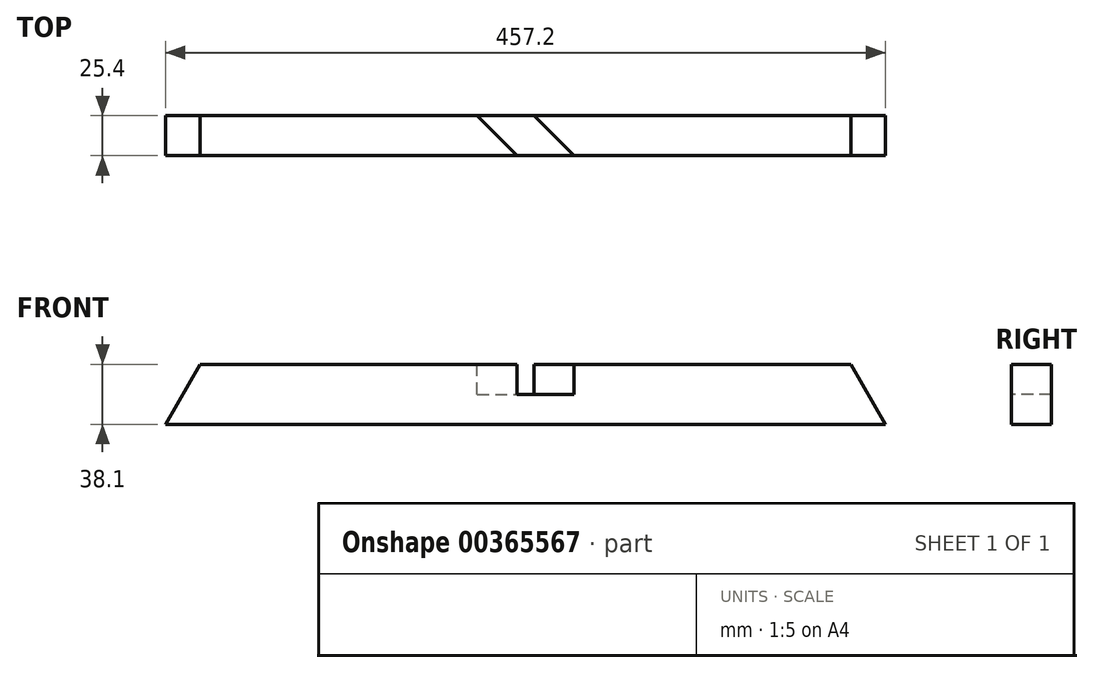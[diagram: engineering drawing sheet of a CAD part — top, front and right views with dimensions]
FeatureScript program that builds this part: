
annotation { "Feature Type Name" : "Feature", "Feature Type Description" : "" }
export const myFeature = defineFeature(function(context is Context, id is Id, definition is map)
    precondition{}
    {
        {
            var Q0;
            Q0=qCreatedBy(makeId("Front.planeOp"),FACE);
            var sketch = newSketch(context, id + "F0", { "sketchPlane" : qUnion([Q0])});
            skLineSegment(sketch, "E0.bottom", {"start": v(0, 0) * mm, "end": v(457.2, 0) * mm});
            skLineSegment(sketch, "E0.top", {"start": v(22, 38.1) * mm, "end": v(435.2, 38.1) * mm});
            skLineSegment(sketch, "E1", {"start": v(0, 0) * mm, "end": v(22, 38.1) * mm});
            skLineSegment(sketch, "E2", {"start": v(457.2, 0) * mm, "end": v(435.2, 38.1) * mm});
            skSolve(sketch);
        }
        {
            var Q0;
            Q0=makeQuery(id+"F0.imprint","IMPRINT",FACE,{"disambiguationData":[TD([[makeQuery(id+"F0.imprint","IMPRINT",EDGE,{"derivedFrom":sQuery(id+"F0.wireOp",EDGE,"E0.bottom")}),1.0]])]});
            extrude(context, id + "F1", {"entities" : qUnion([Q0]), "depth" : 25.4 * mm});
        }
        {
            var Q0;
            Q0=makeQuery(id+"F1.opExtrude","SWEPT_FACE",FACE,{"disambiguationData":[OSD([sQuery(id+"F0.wireOp",EDGE,"E0.top")])]});
            var sketch = newSketch(context, id + "F2", { "sketchPlane" : qUnion([Q0])});
            skLineSegment(sketch, "E3", {"start": v(197.94, 0) * mm, "end": v(223.34, -25.4) * mm});
            skLineSegment(sketch, "E4", {"start": v(223.34, -25.4) * mm, "end": v(259.26, -25.4) * mm});
            skLineSegment(sketch, "E5", {"start": v(259.26, -25.4) * mm, "end": v(233.86, 0) * mm});
            skLineSegment(sketch, "E6", {"start": v(233.86, 0) * mm, "end": v(197.94, 0) * mm});
            skCircle(sketch, "E7", {"center": v(228.6, -12.7) * mm, "radius": 12.7 * mm, "construction": true});
            skSolve(sketch);
        }
        {
            var Q0;
            Q0=makeQuery(id+"F2.imprint","IMPRINT",FACE,{"disambiguationData":[TD([[makeQuery(id+"F2.imprint","IMPRINT",EDGE,{"derivedFrom":sQuery(id+"F2.wireOp",EDGE,"E3")}),1.0]])]});
            var Q1;
            Q1=sQuery(id+"F2.wireOp",EDGE,"E7");
            var Q2;
            Q2=sQuery(id+"F2.wireOp",EDGE,"E5");
            var Q3;
            Q3=sQuery(id+"F2.wireOp",EDGE,"E4");
            var Q4;
            Q4=sQuery(id+"F2.wireOp",EDGE,"E3");
            var Q5;
            Q5=sQuery(id+"F2.wireOp",EDGE,"E6");
            extrude(context, id + "F3", {"entities" : qUnion([Q0]), "operationType" : NewBodyOperationType.REMOVE, "surfaceEntities" : qUnion([Q1, Q2, Q3, Q4, Q5]), "oppositeDirection" : true, "depth" : 19.05 * mm});
        }
    });
